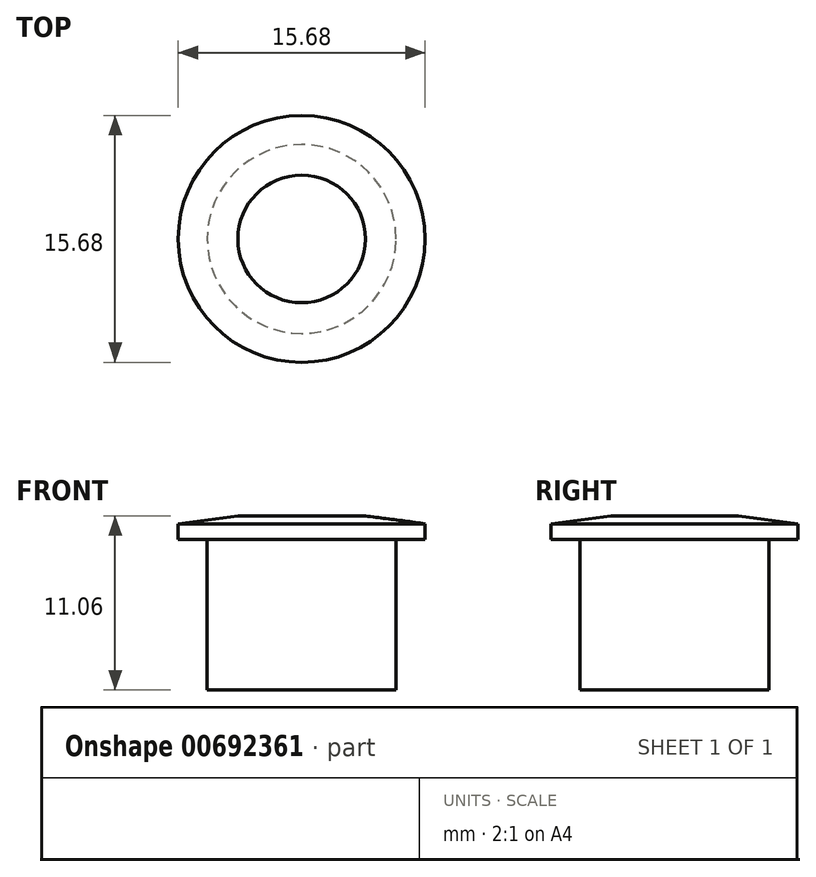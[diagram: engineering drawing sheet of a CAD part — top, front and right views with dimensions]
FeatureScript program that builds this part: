
annotation { "Feature Type Name" : "Feature", "Feature Type Description" : "" }
export const myFeature = defineFeature(function(context is Context, id is Id, definition is map)
    precondition{}
    {
        {
            var Q0;
            Q0=qCreatedBy(makeId("Front.planeOp"),FACE);
            var sketch = newSketch(context, id + "F0", { "sketchPlane" : qUnion([Q0])});
            skLineSegment(sketch, "E0", {"start": v(0, 18.29) * mm, "end": v(-4.05, 18.29) * mm});
            skLineSegment(sketch, "E1", {"start": v(-4.05, 18.29) * mm, "end": v(-7.84, 17.79) * mm});
            skLineSegment(sketch, "E2", {"start": v(-7.84, 17.79) * mm, "end": v(-7.84, 16.79) * mm});
            skLineSegment(sketch, "E3", {"start": v(-7.84, 16.79) * mm, "end": v(-6, 16.79) * mm});
            skLineSegment(sketch, "E4", {"start": v(-6, 16.79) * mm, "end": v(-6, 7.23) * mm});
            skLineSegment(sketch, "E5", {"start": v(-6, 7.23) * mm, "end": v(0, 7.23) * mm});
            skLineSegment(sketch, "E6", {"start": v(0, 43.48) * mm, "end": v(0, -35.72) * mm, "construction": true});
            skLineSegment(sketch, "E7", {"start": v(0, 18.29) * mm, "end": v(0, 7.23) * mm});
            skSolve(sketch);
        }
        {
            var Q0;
            Q0 = qSketchRegion(id + "F0", true);
            var Q1;
            Q1=sQuery(id+"F0.wireOp",EDGE,"E6");
            revolve(context, id + "F1", {"surfaceOperationType" : NewSurfaceOperationType.NEW, "entities" : qUnion([Q0]), "axis" : qUnion([Q1]), "revolveType" : RevolveType.FULL});
        }
    });
